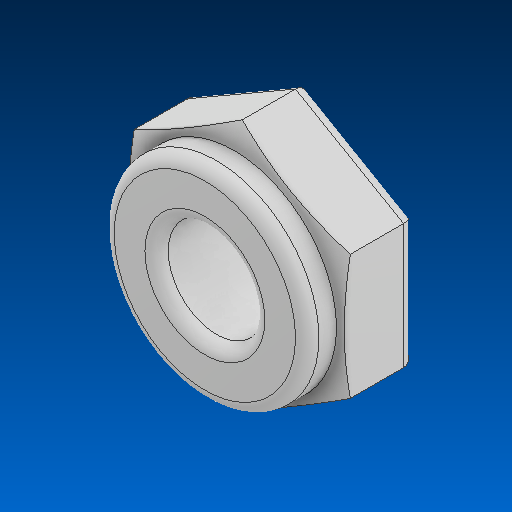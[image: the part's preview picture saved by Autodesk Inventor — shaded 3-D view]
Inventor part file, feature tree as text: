
AUTODESK INVENTOR PART (.ipt)
format: ipt  version: 2022.2 (Build 262287000, 287)  size: 161,280 bytes
history: native  units: in
note: dims shown in document units (in); Inventor stores cm internally (conversion verified against a paired STEP export)
features: fillet x1
ambient origin geometry x8: Origin, YZ Plane, XZ Plane, XY Plane, X Axis, Y Axis, Z Axis, Center Point
bodies: Solid1 (feature_tree)
feature tree (1):
  fillet  "Fillet4"  [1 undecoded]
note: 1 required parameter value undecoded (feature->parameter linkage not recoverable at this tier; creation-order binding heuristic only, values carry confidence <= 0.55)
